annotation { "Feature Type Name" : "Feature", "Feature Type Description" : "" }
export const myFeature = defineFeature(function(context is Context, id is Id, definition is map)
    precondition{}
    {
        {
            var Q0;
            Q0=qCreatedBy(makeId("Front.planeOp"),FACE);
            var sketch = newSketch(context, id + "F0", { "sketchPlane" : qUnion([Q0])});
            skLineSegment(sketch, "E0", {"start": v(0, 0) * mm, "end": v(6.35, 0) * mm});
            skLineSegment(sketch, "E1", {"start": v(6.35, 0) * mm, "end": v(7.45, 6.25) * mm});
            skLineSegment(sketch, "E2", {"start": v(0, 0) * mm, "end": v(-15.87, 27.5) * mm});
            skLineSegment(sketch, "E3", {"start": v(-15.87, 27.5) * mm, "end": v(-22.22, 27.5) * mm});
            skLineSegment(sketch, "E4.1", {"start": v(9.01, -3.18) * mm, "end": v(10.58, 5.7) * mm});
            skLineSegment(sketch, "E4.2", {"start": v(-1.83, -3.18) * mm, "end": v(9.01, -3.18) * mm});
            skLineSegment(sketch, "E4.3", {"start": v(-1.83, -3.18) * mm, "end": v(-17.7, 24.32) * mm});
            skLineSegment(sketch, "E4.4", {"start": v(-17.7, 24.32) * mm, "end": v(-19.56, 24.32) * mm});
            skLineSegment(sketch, "E5", {"start": v(7.45, 6.25) * mm, "end": v(10.58, 5.7) * mm});
            skPoint(sketch, "E6", {"position": v(-27.63, -3.17) * mm});
            skLineSegment(sketch, "E7", {"start": v(-22.22, 27.5) * mm, "end": v(-27.63, -3.17) * mm});
            skPoint(sketch, "E8", {"position": v(-19.56, 24.32) * mm});
            skLineSegment(sketch, "E9", {"start": v(-27.63, -3.17) * mm, "end": v(-24.4, -3.17) * mm});
            skPoint(sketch, "E10", {"position": v(-24.4, -3.17) * mm});
            skLineSegment(sketch, "E11", {"start": v(-19.56, 24.32) * mm, "end": v(-24.4, -3.17) * mm});
            skSolve(sketch);
        }
        {
            assignVariable(context, id + "F1", {"name" : "HoldW", "anyValue" : 3.25});
        }
        {
            var Q0;
            Q0=makeQuery(id+"F0.imprint","IMPRINT",FACE,{"disambiguationData":[TD([[makeQuery(id+"F0.imprint","IMPRINT",EDGE,{"derivedFrom":sQuery(id+"F0.wireOp",EDGE,"E0")}),-1.0]])]});
            extrude(context, id + "F2", {"entities" : qUnion([Q0]), "depth" : (getVariable(context, 'HoldW')) * mm, "offsetDistance" : 25.4 * mm});
        }
        {
            var Q0;
            Q0=makeQuery(id+"F2.opExtrude","SWEPT_FACE",FACE,{"disambiguationData":[OSD([sQuery(id+"F0.wireOp",EDGE,"E3")])]});
            extrude(context, id + "F3", {"entities" : qUnion([Q0]), "operationType" : NewBodyOperationType.ADD, "depth" : 63.5 * mm, "offsetDistance" : 25.4 * mm});
        }
        {
            var Q0;
            Q0=makeQuery(id+"F3.opExtrude","SWEPT_FACE",FACE,{"disambiguationData":[OSD([sQuery(id+"F0.wireOp",EDGE,"E2"),sQuery(id+"F0.wireOp",EDGE,"E3")])]});
            var sketch = newSketch(context, id + "F4", { "sketchPlane" : qUnion([Q0])});
            skText(sketch, "E12", { "text": "R I T", "fontName": "NotoSansCJKjp-Regular.otf"});
            const initialGuessF4  = {"E12": [-0.08255, 0.0275, 1, 0, 0.02972]};
            skSetInitialGuess(sketch, initialGuessF4);
            skSolve(sketch);
        }
        {
            var Q0;
            {var subQ2=sQuery(id+"F4.wireOp",EDGE,"E12.sketch_text.stroke-5");Q0=makeQuery(id+"F4.imprint","IMPRINT",FACE,{"disambiguationData":[TD([[makeQuery(id+"F4.imprint","IMPRINT",EDGE,{"derivedFrom":subQ2}),-1.0]])]});}
            var Q1;
            Q1=makeQuery(id+"F4.imprint","IMPRINT",FACE,{"disambiguationData":[TD([[makeQuery(id+"F4.imprint","IMPRINT",EDGE,{"derivedFrom":sQuery(id+"F4.wireOp",EDGE,"E12.sketch_text.stroke-0")}),-1.0]])]});
            var Q2;
            {var subQ0=sQuery(id+"F4.wireOp",EDGE,"E12.sketch_text.stroke-11");Q2=makeQuery(id+"F4.imprint","IMPRINT",FACE,{"disambiguationData":[TD([[makeQuery(id+"F4.imprint","IMPRINT",EDGE,{"derivedFrom":subQ0}),-1.0]])]});}
            extrude(context, id + "F5", {"entities" : qUnion([Q0, Q1, Q2]), "operationType" : NewBodyOperationType.REMOVE, "endBound" : BoundingType.THROUGH_ALL, "oppositeDirection" : true, "depth" : 25.4 * mm, "offsetDistance" : 25.4 * mm});
        }
        {
            var Q0;
            Q0=makeQuery(id+"F2.opExtrude","SWEPT_FACE",FACE,{"disambiguationData":[OSD([sQuery(id+"F0.wireOp",EDGE,"E7")])]});
            var sketch = newSketch(context, id + "F6", { "sketchPlane" : qUnion([Q0])});
            skText(sketch, "E13", { "text": "Ben Bellantoni\nColby Benway\n", "fontName": "OpenSans-Regular.ttf"});
            const initialGuessF6  = {"E13": [0.00029, -0.00123, 1, 0, 0.00252]};
            skSetInitialGuess(sketch, initialGuessF6);
            skSolve(sketch);
        }
        {
            var Q0;
            Q0 = qSketchRegion(id + "F6", true);
            extrude(context, id + "F7", {"entities" : qUnion([Q0]), "operationType" : NewBodyOperationType.REMOVE, "oppositeDirection" : true, "depth" : 1.59 * mm, "offsetDistance" : 25.4 * mm});
        }
    });